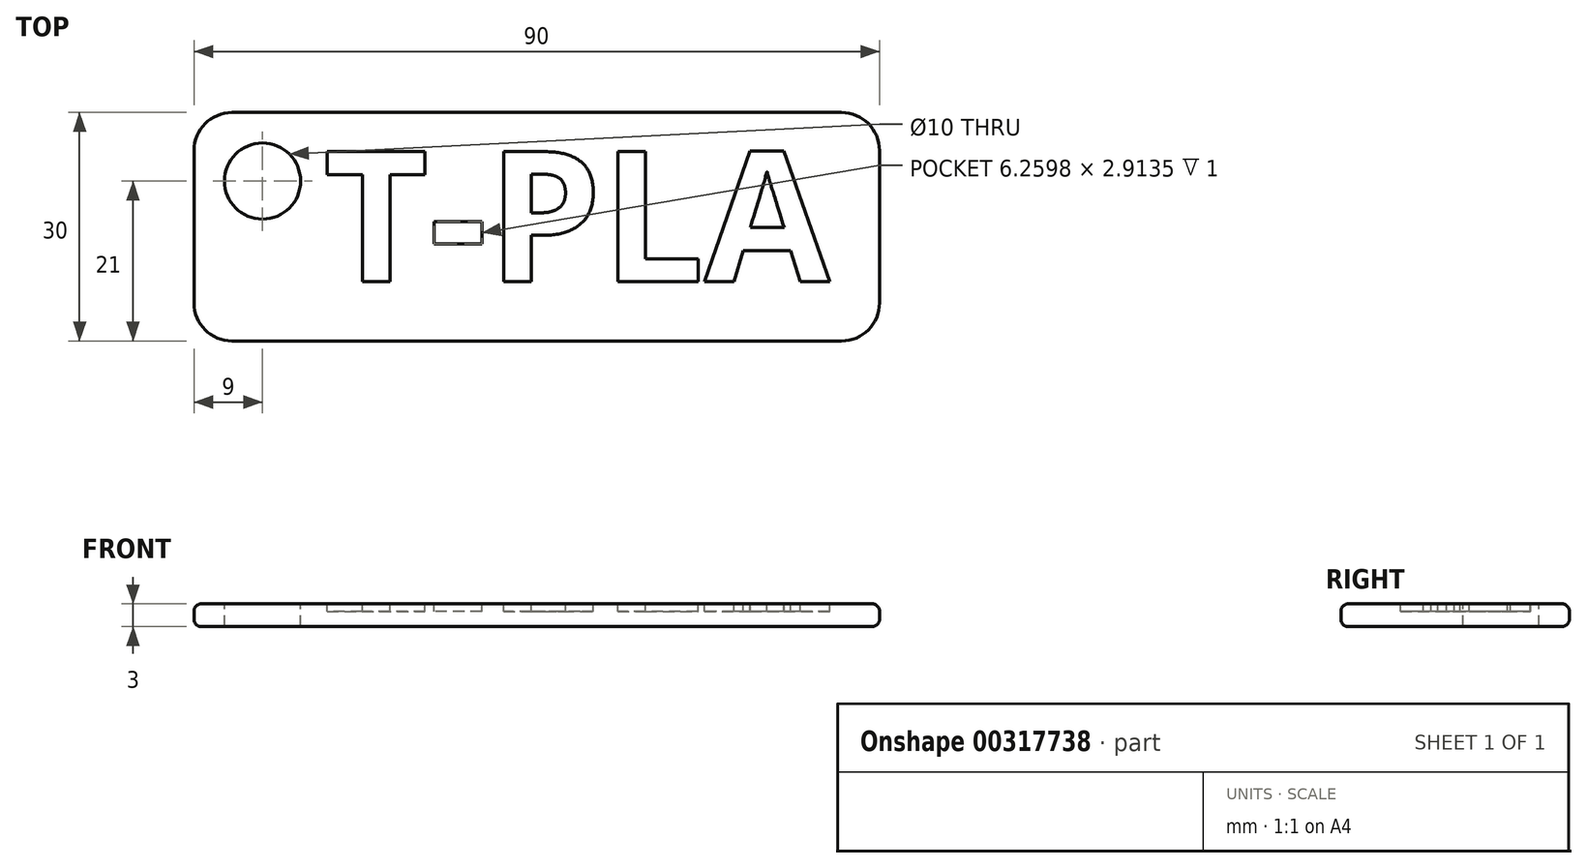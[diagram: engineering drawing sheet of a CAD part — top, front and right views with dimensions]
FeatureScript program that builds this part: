
annotation { "Feature Type Name" : "Feature", "Feature Type Description" : "" }
export const myFeature = defineFeature(function(context is Context, id is Id, definition is map)
    precondition{}
    {
        {
            var Q0;
            Q0=qCreatedBy(makeId("Top.planeOp"),FACE);
            var sketch = newSketch(context, id + "F0", { "sketchPlane" : qUnion([Q0])});
            skLineSegment(sketch, "E0.bottom", {"start": v(-45, 15) * mm, "end": v(45, 15) * mm});
            skLineSegment(sketch, "E0.top", {"start": v(-45, -15) * mm, "end": v(45, -15) * mm});
            skLineSegment(sketch, "E0.left", {"start": v(-45, 15) * mm, "end": v(-45, -15) * mm});
            skLineSegment(sketch, "E0.right", {"start": v(45, 15) * mm, "end": v(45, -15) * mm});
            skLineSegment(sketch, "E1", {"start": v(-45, 15) * mm, "end": v(45, -15) * mm, "construction": true});
            skSolve(sketch);
        }
        {
            var Q0;
            Q0=makeQuery(id+"F0.imprint","IMPRINT",FACE,{"disambiguationData":[TD([[makeQuery(id+"F0.imprint","IMPRINT",EDGE,{"derivedFrom":sQuery(id+"F0.wireOp",EDGE,"E0.bottom")}),-1.0]])]});
            extrude(context, id + "F1", {"entities" : qUnion([Q0]), "depth" : 3 * mm});
        }
        {
            var Q0;
            Q0=makeQuery(id+"F1.opExtrude","CAP_FACE",FACE,{"disambiguationData":[OSD([sQuery(id+"F0.wireOp",EDGE,"E0.bottom"),sQuery(id+"F0.wireOp",EDGE,"E0.top"),sQuery(id+"F0.wireOp",EDGE,"E0.left"),sQuery(id+"F0.wireOp",EDGE,"E0.right")])],"isStart":false});
            var Q1;
            Q1=makeQuery(id+"F1.opExtrude","CAP_FACE",FACE,{"disambiguationData":[OSD([sQuery(id+"F0.wireOp",EDGE,"E0.bottom"),sQuery(id+"F0.wireOp",EDGE,"E0.top"),sQuery(id+"F0.wireOp",EDGE,"E0.left"),sQuery(id+"F0.wireOp",EDGE,"E0.right")])],"isStart":true});
            fillet(context, id + "F2", {"entities" : qUnion([Q0, Q1]), "radius" : 1 * mm, "tangentPropagation" : true, "allowEdgeOverflow" : false});
        }
        {
            var Q0;
            Q0=makeQuery(id+"F1.opExtrude","SWEPT_EDGE",EDGE,{"disambiguationData":[OSD([sQuery(id+"F0.wireOp",EDGE,"E0.top"),sQuery(id+"F0.wireOp",EDGE,"E0.right")])]});
            var Q1;
            Q1=makeQuery(id+"F1.opExtrude","SWEPT_EDGE",EDGE,{"disambiguationData":[OSD([sQuery(id+"F0.wireOp",EDGE,"E0.bottom"),sQuery(id+"F0.wireOp",EDGE,"E0.right")])]});
            var Q2;
            Q2=makeQuery(id+"F1.opExtrude","SWEPT_EDGE",EDGE,{"disambiguationData":[OSD([sQuery(id+"F0.wireOp",EDGE,"E0.bottom"),sQuery(id+"F0.wireOp",EDGE,"E0.left")])]});
            var Q3;
            Q3=makeQuery(id+"F1.opExtrude","SWEPT_EDGE",EDGE,{"disambiguationData":[OSD([sQuery(id+"F0.wireOp",EDGE,"E0.top"),sQuery(id+"F0.wireOp",EDGE,"E0.left")])]});
            fillet(context, id + "F3", {"entities" : qUnion([Q0, Q1, Q2, Q3]), "radius" : 5 * mm, "tangentPropagation" : true, "allowEdgeOverflow" : false});
        }
        {
            var Q0;
            {var subQ0=sQuery(id+"F0.wireOp",EDGE,"E0.left");var subQ2=sQuery(id+"F0.wireOp",EDGE,"E0.bottom");var subQ4=sQuery(id+"F0.wireOp",EDGE,"E0.right");var subQ6=sQuery(id+"F0.wireOp",EDGE,"E0.top");Q0=makeQuery(id+"FmQCBBX3Ub0qneL_1.boolean.opBoolean","SPLIT",FACE,{"disambiguationData":[TD([makeQuery(id+"FmQCBBX3Ub0qneL_1.opExtrude","SWEPT_FACE",FACE,{"disambiguationData":[OSD([sQuery(id+"FOCoeRmDbjhRCuz_1.wireOp",EDGE,"4a1fb44a-e7be-4e23-9449-000d953c446c.sketch_text.stroke-0")])]})])],"derivedFrom":makeQuery(id+"F1.opExtrude","CAP_FACE",FACE,{"disambiguationData":[OSD([subQ2,subQ6,subQ0,subQ4])],"isStart":false})});}
            var sketch = newSketch(context, id + "F4", { "sketchPlane" : qUnion([Q0])});
            skCircle(sketch, "E2", {"center": v(-36, 6) * mm, "radius": 5 * mm});
            skSolve(sketch);
        }
        {
            var Q0;
            Q0=qSketchRegion(id+"F4",true);
            extrude(context, id + "F5", {"entities" : qUnion([Q0]), "operationType" : NewBodyOperationType.REMOVE, "oppositeDirection" : true, "depth" : 3 * mm});
        }
        {
            var Q0;
            Q0=makeQuery(id+"F1.opExtrude","CAP_FACE",FACE,{"disambiguationData":[OSD([sQuery(id+"F0.wireOp",EDGE,"E0.bottom"),sQuery(id+"F0.wireOp",EDGE,"E0.top"),sQuery(id+"F0.wireOp",EDGE,"E0.left"),sQuery(id+"F0.wireOp",EDGE,"E0.right")])],"isStart":false});
            var sketch = newSketch(context, id + "F6", { "sketchPlane" : qUnion([Q0])});
            skText(sketch, "E3", { "text": "T-PLA", "fontName": "OpenSans-Bold.ttf"});
            const initialGuessF6  = {"E3": [-0.028, -0.00719, 1, 0, 0.01719]};
            skSetInitialGuess(sketch, initialGuessF6);
            skSolve(sketch);
        }
        {
            var Q0;
            Q0=qSketchRegion(id+"F6",true);
            extrude(context, id + "F7", {"entities" : qUnion([Q0]), "operationType" : NewBodyOperationType.REMOVE, "oppositeDirection" : true, "depth" : 1 * mm});
        }
    });
